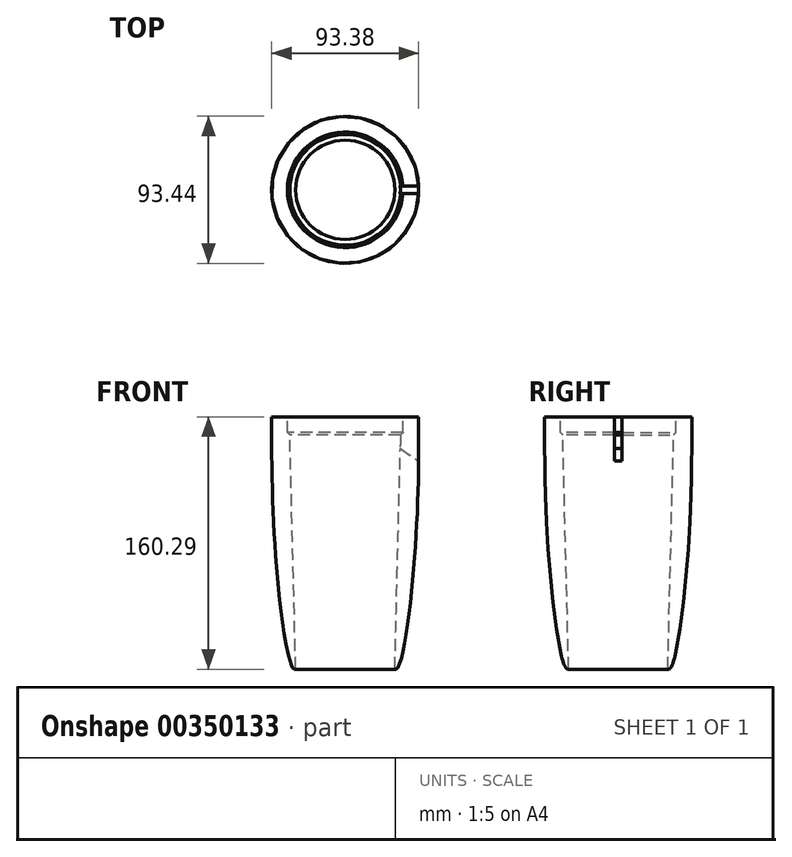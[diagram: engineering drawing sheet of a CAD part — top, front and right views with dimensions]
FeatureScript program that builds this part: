
annotation { "Feature Type Name" : "Feature", "Feature Type Description" : "" }
export const myFeature = defineFeature(function(context is Context, id is Id, definition is map)
    precondition{}
    {
        {
            var Q0;
            Q0=qCreatedBy(makeId("Front.planeOp"),FACE);
            var sketch = newSketch(context, id + "F0", { "sketchPlane" : qUnion([Q0])});
            skLineSegment(sketch, "E0", {"start": v(36.7, 0) * mm, "end": v(36.7, -10) * mm});
            skLineSegment(sketch, "E1", {"start": v(36.7, 0) * mm, "end": v(46.7, 0) * mm});
            skLineSegment(sketch, "E2", {"start": v(46.7, 0) * mm, "end": v(46.7, -10) * mm});
            skLineSegment(sketch, "E3", {"start": v(36.7, -10) * mm, "end": v(35.2, -11.5) * mm});
            skLineSegment(sketch, "E4", {"start": v(35.2, -11.5) * mm, "end": v(31.5, -160) * mm});
            skFitSpline(sketch, "E5", {"points": [v(31.5, -160) * mm, v(41.72, -115.07) * mm, v(46.7, -10) * mm], "startDerivative": vector(25.76, -23.9) * mm, "endDerivative": vector(-0.99, 136.93) * mm});
            skLineSegment(sketch, "E6", {"start": v(0, 2.49) * mm, "end": v(0, -160.77) * mm});
            skSolve(sketch);
        }
        {
            var Q0;
            Q0=makeQuery(id+"F0.imprint","IMPRINT",FACE,{"disambiguationData":[TD([[makeQuery(id+"F0.imprint","IMPRINT",EDGE,{"derivedFrom":sQuery(id+"F0.wireOp",EDGE,"E0")}),1.0]])]});
            var Q1;
            Q1=sQuery(id+"F0.wireOp",EDGE,"E6");
            revolve(context, id + "F1", {"entities" : qUnion([Q0]), "axis" : qUnion([Q1]), "revolveType" : RevolveType.FULL});
        }
        {
            var Q0;
            Q0=makeQuery(id+"F1.opRevolve","SWEPT_FACE",FACE,{"disambiguationData":[OSD([sQuery(id+"F0.wireOp",EDGE,"E1")])]});
            var sketch = newSketch(context, id + "F2", { "sketchPlane" : qUnion([Q0])});
            skCircle(sketch, "E7.0.0", {"center": v(0, 0) * mm, "radius": 46.7 * mm});
            skLineSegment(sketch, "E8.bottom", {"start": v(32.37, 2.5) * mm, "end": v(51.98, 2.5) * mm});
            skLineSegment(sketch, "E8.top", {"start": v(32.37, -2.5) * mm, "end": v(51.98, -2.5) * mm});
            skLineSegment(sketch, "E8.left", {"start": v(32.37, 2.5) * mm, "end": v(32.37, -2.5) * mm});
            skLineSegment(sketch, "E8.right", {"start": v(51.98, 2.5) * mm, "end": v(51.98, -2.5) * mm});
            skSolve(sketch);
        }
        {
            var Q0;
            {var subQ5=sQuery(id+"F2.wireOp",EDGE,"E8.right");Q0=makeQuery(id+"F2.imprint","IMPRINT",FACE,{"disambiguationData":[TD([[makeQuery(id+"F2.imprint","IMPRINT",EDGE,{"derivedFrom":subQ5}),-1.0]])]});}
            var Q1;
            {var subQ0=sQuery(id+"F2.wireOp",EDGE,"E8.bottom");var subQ1=sQuery(id+"F2.wireOp",EDGE,"E7.0.0");var subQ2=makeQuery(id+"F2.imprint","INTERSECT",VERTEX,{"derivedFrom":[subQ1,subQ0]});Q1=makeQuery(id+"F2.imprint","IMPRINT",FACE,{"disambiguationData":[TD([[makeQuery(id+"F2.imprint","IMPRINT",EDGE,{"disambiguationData":[TD([[subQ2,1.0]])],"derivedFrom":subQ1}),1.0]])]});}
            var Q2;
            {var subQ0=sQuery(id+"F2.wireOp",EDGE,"E8.left");Q2=makeQuery(id+"F2.imprint","IMPRINT",FACE,{"disambiguationData":[TD([[makeQuery(id+"F2.imprint","IMPRINT",EDGE,{"derivedFrom":subQ0}),1.0]])]});}
            extrude(context, id + "F3", {"entities" : qUnion([Q0, Q1, Q2]), "operationType" : NewBodyOperationType.REMOVE, "oppositeDirection" : true, "depth" : 20 * mm});
        }
        {
            var Q0;
            Q0=makeQuery(id+"F3.boolean.opBoolean","INTERSECT",EDGE,{"derivedFrom":[makeQuery(id+"F1.opRevolve","SWEPT_FACE",FACE,{"disambiguationData":[OSD([sQuery(id+"F0.wireOp",EDGE,"E5")])]}),makeQuery(id+"F3.opExtrude","CAP_FACE",FACE,{"disambiguationData":[OSD([sQuery(id+"F2.wireOp",EDGE,"E8.bottom"),sQuery(id+"F2.wireOp",EDGE,"E8.top"),sQuery(id+"F2.wireOp",EDGE,"E8.left"),sQuery(id+"F2.wireOp",EDGE,"E8.right")])],"isStart":false})]});
            chamfer(context, id + "F4", {"entities" : qUnion([Q0]), "chamferType" : ChamferType.TWO_OFFSETS, "width1" : 12 * mm, "oppositeDirection" : false, "width2" : 8 * mm, "tangentPropagation" : true});
        }
    });
